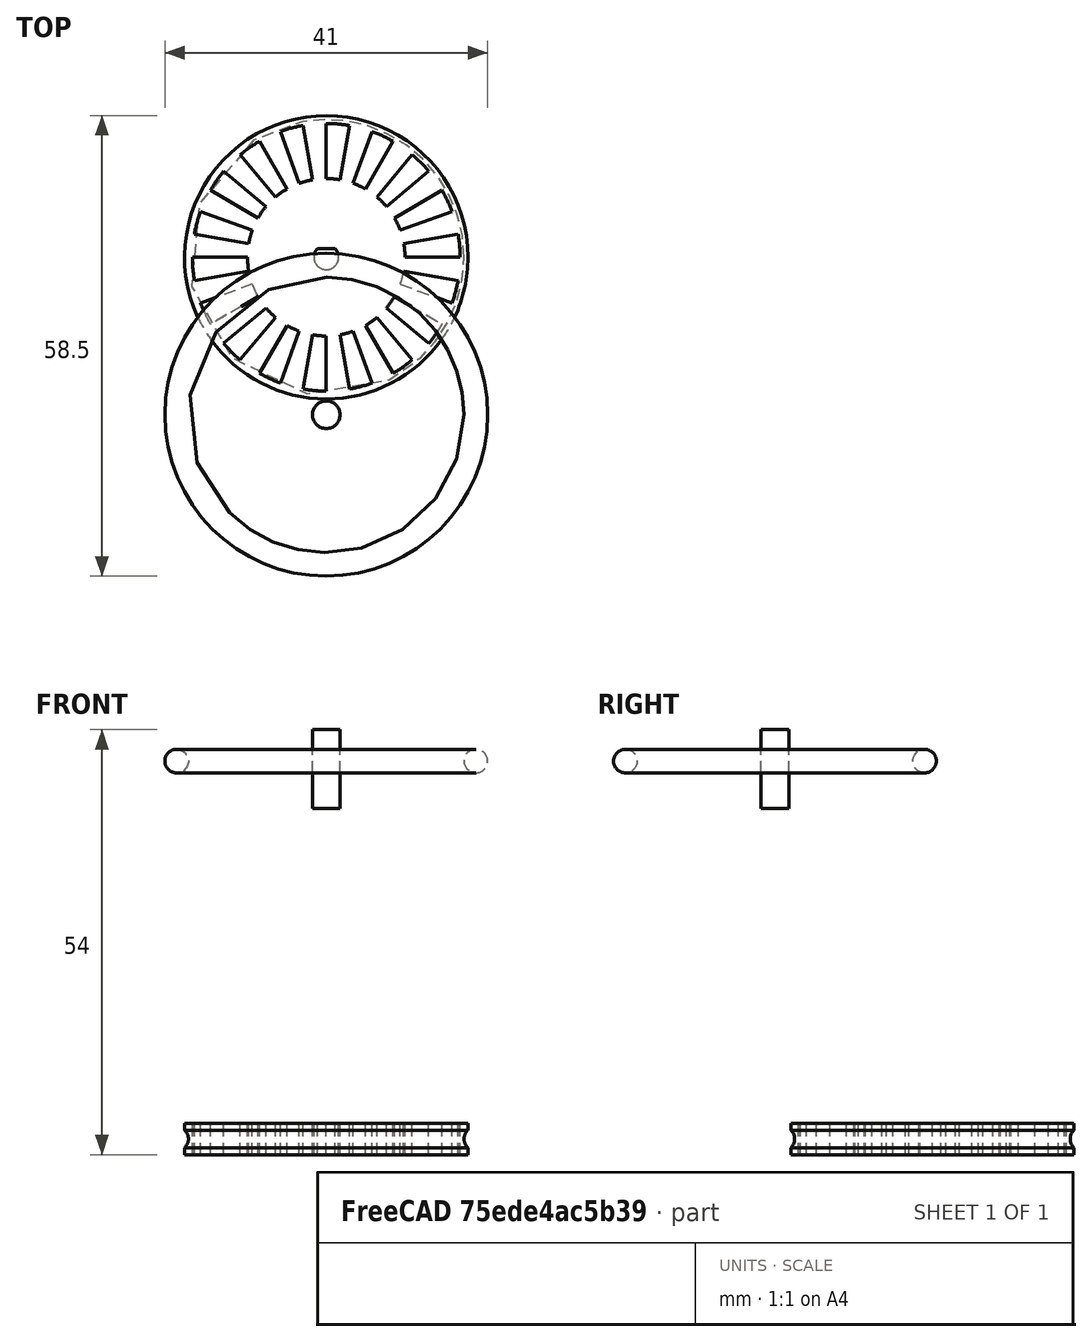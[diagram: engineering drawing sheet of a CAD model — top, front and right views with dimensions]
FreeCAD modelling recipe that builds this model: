
FCSTD DOCUMENT  (FreeCAD 0.17R13522 (Git))
Label: wheel 1.57 hole
License: All rights reserved
LicenseURL: http://en.wikipedia.org/wiki/All_rights_reserved
objects: Part::Feature×17, Part::Cut×7, Part::Cylinder×5, Part::Box×3, Part::Torus×2, Part::MultiFuse×1
note: 35 computed .brp shape members not serialized (recipe doc carries the construction recipe); baked Part::Feature solids carry a one-line shape summary decoded from their .brp

FEATURE [Part::Cylinder] Cylinder012  label="wheel1a"
  Angle = 360
  AttacherType = Attacher::AttachEngine3D
  Height = 4
  Radius = 18
FEATURE [Part::Cylinder] Cylinder028  label="Cylinder024"
  Angle = 360
  AttacherType = Attacher::AttachEngine3D
  Height = 10
  Placement = pos=(0,0,-1) rot=(0,0,1;0rad)
  Radius = 1.57
FEATURE [Part::Box] Box084016  label="Cube067"
  AttacherType = Attacher::AttachEngine3D
  Height = 12
  Length = 10
  Placement = pos=(-5,1.1,-1.5) rot=(0,0,1;0rad)
  Width = 10
FEATURE [Part::Cut] Cut057
  Base = -> Cylinder028
  Tool = -> Box084016
FEATURE [Part::Cut] Cut062
  Base = -> Cylinder012
  Tool = -> Cut057
FEATURE [Part::Torus] Torus002
  Angle1 = -180
  Angle2 = 180
  Angle3 = 360
  AttacherType = Attacher::AttachEngine3D
  Placement = pos=(0,0,2) rot=(0,0,1;0rad)
  Radius1 = 19
  Radius2 = 1.5
FEATURE [Part::Cut] Cut063  label="wheel"
  Base = -> Cut062
  Tool = -> Torus002
FEATURE [Part::Torus] Torus
  Angle1 = -180
  Angle2 = 180
  Angle3 = 360
  AttacherType = Attacher::AttachEngine3D
  Placement = pos=(0,-20,50) rot=(0,0,1;0rad)
  Radius1 = 19
  Radius2 = 1.5
FEATURE [Part::Cylinder] Cylinder062  label="Cylinder158"
  Angle = 360
  AttacherType = Attacher::AttachEngine3D
  Height = 10
  Radius = 17
FEATURE [Part::Cylinder] Cylinder063  label="Cylinder159"
  Angle = 360
  AttacherType = Attacher::AttachEngine3D
  Height = 16
  Placement = pos=(0,0,-4) rot=(0,0,1;0rad)
  Radius = 10
FEATURE [Part::Cut] Cut044
  Base = -> Cylinder062
  Tool = -> Cylinder063
FEATURE [Part::Box] Box026  label="Cube025"
  AttacherType = Attacher::AttachEngine3D
  Height = 20
  Length = 18
  Placement = pos=(0,0,-5) rot=(0,0,1;0rad)
  Width = 20
FEATURE [Part::Box] Box027  label="Cube026"
  AttacherType = Attacher::AttachEngine3D
  Height = 20
  Length = 10
  Placement = pos=(0,0,-5) rot=(0,0,1;0.174533rad)
  Width = 20
FEATURE [Part::Cut] Cut045
  Base = -> Box027
  Tool = -> Box026
FEATURE [Part::Feature] Cut045001
  Placement = pos=(0,0,0) rot=(0,0,1;0.349066rad)
  shape: bbox 10 x 22.32 x 20 mm, 7 faces (baked)
FEATURE [Part::Feature] Cut045002
  Placement = pos=(0,0,0) rot=(0,0,1;0.698132rad)
  shape: bbox 15.32 x 20.52 x 20 mm, 7 faces (baked)
FEATURE [Part::Feature] Cut045003
  Placement = pos=(0,0,0) rot=(0,0,1;1.0472rad)
  shape: bbox 18.79 x 16.24 x 20 mm, 7 faces (baked)
FEATURE [Part::Feature] Cut045004
  Placement = pos=(0,0,0) rot=(0,0,1;1.39626rad)
  shape: bbox 20 x 10 x 20 mm, 7 faces (baked)
FEATURE [Part::Feature] Cut045005
  Placement = pos=(0,0,0) rot=(0,0,1;1.74533rad)
  shape: bbox 22.21 x 9.894 x 20 mm, 7 faces (baked)
FEATURE [Part::Feature] Cut045006
  Placement = pos=(0,0,0) rot=(0,0,1;2.0944rad)
  shape: bbox 21.75 x 12.86 x 20 mm, 7 faces (baked)
FEATURE [Part::Feature] Cut045007
  Placement = pos=(0,0,0) rot=(0,0,1;2.44346rad)
  shape: bbox 18.66 x 17.32 x 20 mm, 7 faces (baked)
FEATURE [Part::Feature] Cut045008
  Placement = pos=(0,0,0) rot=(0,0,1;2.79253rad)
  shape: bbox 13.32 x 19.7 x 20 mm, 7 faces (baked)
FEATURE [Part::Feature] Cut045009
  Placement = pos=(0,0,0) rot=(0,0,1;3.14159rad)
  shape: bbox 10.1 x 21.43 x 20 mm, 7 faces (baked)
FEATURE [Part::Feature] Cut045010
  Placement = pos=(0,0,0) rot=(0,0,1;3.49066rad)
  shape: bbox 10 x 22.32 x 20 mm, 7 faces (baked)
FEATURE [Part::Feature] Cut045011
  Placement = pos=(0,0,0) rot=(0,0,1;3.83972rad)
  shape: bbox 15.32 x 20.52 x 20 mm, 7 faces (baked)
FEATURE [Part::Feature] Cut045012
  Placement = pos=(0,0,0) rot=(0,0,1;4.18879rad)
  shape: bbox 18.79 x 16.24 x 20 mm, 7 faces (baked)
FEATURE [Part::Feature] Cut045013
  Placement = pos=(0,0,0) rot=(0,0,-1;1.74533rad)
  shape: bbox 20 x 10 x 20 mm, 7 faces (baked)
FEATURE [Part::Feature] Cut045014
  Placement = pos=(0,0,0) rot=(0,0,-1;1.39626rad)
  shape: bbox 22.21 x 9.894 x 20 mm, 7 faces (baked)
FEATURE [Part::Feature] Cut045015
  Placement = pos=(0,0,0) rot=(0,0,-1;1.0472rad)
  shape: bbox 21.75 x 12.86 x 20 mm, 7 faces (baked)
FEATURE [Part::Feature] Cut045016
  Placement = pos=(0,0,0) rot=(0,0,-1;0.698132rad)
  shape: bbox 18.66 x 17.32 x 20 mm, 7 faces (baked)
FEATURE [Part::Feature] Cut045017
  Placement = pos=(0,0,0) rot=(0,0,-1;0.349066rad)
  shape: bbox 13.32 x 19.7 x 20 mm, 7 faces (baked)
FEATURE [Part::MultiFuse] Fusion095
  Shapes = -> [Cut045001,Cut045008,Cut045010,Cut045009,Cut045005,Cut045003,Cut045006,Cut045002,Cut045004,Cut045007,Cut045016,Cut045017,Cut045011,Cut045012,Cut045013,Cut045014,Cut045015,Cut045]
FEATURE [Part::Cut] Cut045018
  Base = -> Cut044
  Placement = pos=(0,0,-1) rot=(0,1,0;0rad)
  Tool = -> Fusion095
FEATURE [Part::Cylinder] Cylinder064  label="Cylinder160"
  Angle = 360
  AttacherType = Attacher::AttachEngine3D
  Height = 10
  Placement = pos=(0,-20,44) rot=(0,0,1;0rad)
  Radius = 1.75
FEATURE [Part::Cut] Cut
  Base = -> Cut063
  Tool = -> Cut045018
